# Revit family: Holocom-Enclosures-2015
name_source: partatom
category: Security Devices
revit_build: Autodesk Revit 2015 (Build: 20140606_1530(x64)
units: mm (PartAtom-declared; Revit-internal decimal feet)

## types (16) — shared parameters
Default Elevation = 4' - 0"
Manufacturer = Holocom
Material = Holocom_WhiteTextured
URL = www.holocom.com

## per-type parameters (varying)
| type | Depth | Height | High Security Pull Box | Latch | Model | Padlock Hasp | Product Notes | Product Page URL | Width |
| Pull Box PB01 | 0' - 4" | 1' - 0" | Yes | Yes | SEC-WM-PB1 | Yes | Available in 16 gauge and 12 gauge steel | http://www.holocom.com | 1' - 6" |
| Pull Box PB02 | 0' - 6" | 1' - 4" | Yes | Yes | SEC-WM-PB2 | Yes | Available in 16 gauge and 12 gauge steel | http://www.holocom.com | 2' - 0" |
| Pull Box PB03 | 0' - 6" | 2' - 0" | No | No | SEC-WM-PB3 | No | Available in 16 gauge and 12 gauge steel | http://www.holocom.com | 2' - 0" |
| Pull Box PB05 | 0' - 6" | 1' - 0" | Yes | Yes | SEC-WM-PB5 | Yes | 16 gauge steel | http://www.holocom.com | 1' - 6" |
| Pull Box PB09 | 0' - 9" | 3' - 0" | Yes | Yes | SEC-WM-PB9 | Yes | 16 gauge steel | http://www.holocom.com | 2' - 6" |
| Pull Box PB04 H1 | 1' - 0" | 2' - 0" | Yes | Yes | SEC-WM-PB4-H1 | Yes | 16 gauge steel | TBD | 2' - 0" |
| Pull Box PB04 H5 | 0' - 10" | 2' - 0" | Yes | Yes | SEC-WM-PB4-H5 | Yes | 12 gauge steel | http://www.holocom.com | 2' - 0" |
| Pull Box PB06 | 0' - 8" | 3' - 4" | Yes | Yes | SEC-WM-PB6-H1 | Yes | 16 gauge steel | TBD | 5' - 0" |
| Pull Box PB08 | 0' - 10" | 2' - 0" | Yes | Yes | SEC-WM-PB8 | Yes | 16 gauge steel | TBD | 2' - 0" |
| Pull Box PB10 | 0' - 10" | 0' - 5" | Yes | Yes | SEC-WM-PB10 | Yes | 16 gauge steel | TBD | 0' - 5" |
| Pull Box PB11 | 0' - 2 29/32" | 3' - 0" | Yes | Yes | SEC-WM-PB11 | Yes | 16 gauge steel | TBD | 2' - 5" |
| Enclosure 118 | 0' - 8" | 1' - 0" | Yes | No | SEC-WM-118 | Yes | Available in 16 gauge and 12 gauge steel | http://www.holocom.com | 1' - 0" |
| Enclosure 885 | 0' - 5" | 0' - 8" | Yes | No | SEC-WM-885 | Yes | Available in 16 gauge and 12 gauge steel | http://www.holocom.com | 0' - 8" |
| Enclosure 764 | 0' - 4 1/2" | 0' - 7 1/2" | Yes | No | SEC-WM-764 | Yes | Available in 16 gauge and 12 gauge steel | http://www.holocom.com | 0' - 6" |
| Secure Wall Mount Enclosure | 0' - 9 1/2" | 3' - 6" | Yes | Yes | SEC-WM-04U | Yes | 16 gauge steel | http://www.holocom.com | 2' - 5" |
| User Drop Box | 0' - 9 1/2" | 3' - 6" | No | No | SEC-WM-UDB | No | 16 gauge steel | http://www.holocom.com | 2' - 5" |

## geometry (parser evidence)
native form markers: Sweep x10
no freeform markers — native parametric forms only
